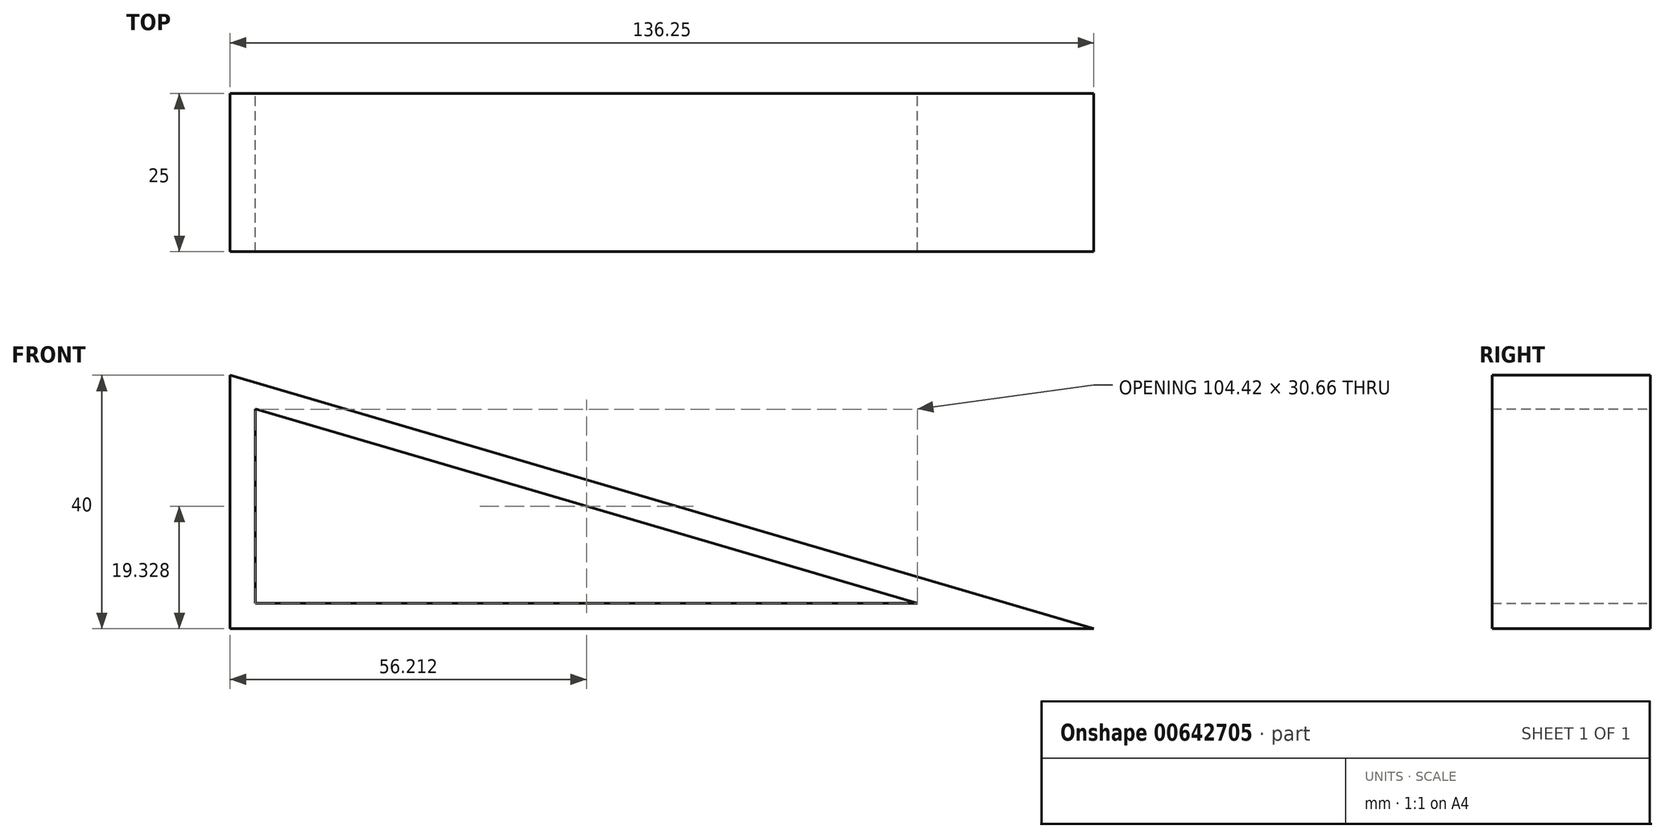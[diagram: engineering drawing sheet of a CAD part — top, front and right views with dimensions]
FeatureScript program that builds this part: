
annotation { "Feature Type Name" : "Feature", "Feature Type Description" : "" }
export const myFeature = defineFeature(function(context is Context, id is Id, definition is map)
    precondition{}
    {
        {
            var Q0;
            Q0=qCreatedBy(makeId("Front.planeOp"),FACE);
            var sketch = newSketch(context, id + "F0", { "sketchPlane" : qUnion([Q0])});
            skLineSegment(sketch, "E0", {"start": v(0, 0) * mm, "end": v(0, 40) * mm});
            skLineSegment(sketch, "E1", {"start": v(0, 40) * mm, "end": v(136.25, 0) * mm});
            skLineSegment(sketch, "E2", {"start": v(136.25, 0) * mm, "end": v(0, 0) * mm});
            skSolve(sketch);
        }
        {
            var Q0;
            Q0=makeQuery(id+"F0.imprint","IMPRINT",FACE,{"disambiguationData":[TD([[makeQuery(id+"F0.imprint","IMPRINT",EDGE,{"derivedFrom":sQuery(id+"F0.wireOp",EDGE,"E0")}),-1.0]])]});
            extrude(context, id + "F1", {"entities" : qUnion([Q0]), "depth" : 33 * mm, "offsetDistance" : 25 * mm});
        }
        {
            var Q0;
            Q0=makeQuery(id+"F1.opExtrude","SWEPT_BODY",BODY,{"disambiguationData":[OSD([sQuery(id+"F0.wireOp",EDGE,"E0"),sQuery(id+"F0.wireOp",EDGE,"E1"),sQuery(id+"F0.wireOp",EDGE,"E2")])]});
            var Q1;
            Q1=sQuery(id+"F0.wireOp",EDGE,"E2");
            transform(context, id + "F2", {"entities" : qUnion([Q0]), "transformType" : TransformType.ROTATION, "transformAxis" : qUnion([Q1]), "angle" : 90 * degree, "makeCopy" : false});
        }
        {
            var Q0;
            Q0=makeQuery(id+"F1.opExtrude","CAP_FACE",FACE,{"disambiguationData":[OSD([sQuery(id+"F0.wireOp",EDGE,"E0"),sQuery(id+"F0.wireOp",EDGE,"E1"),sQuery(id+"F0.wireOp",EDGE,"E2")])],"isStart":false});
            var Q1;
            Q1=makeQuery(id+"F1.opExtrude","SWEPT_BODY",BODY,{"disambiguationData":[OSD([sQuery(id+"F0.wireOp",EDGE,"E0"),sQuery(id+"F0.wireOp",EDGE,"E1"),sQuery(id+"F0.wireOp",EDGE,"E2")])]});
            shell(context, id + "F3", {"isHollow" : true, "entities" : qUnion([Q0]), "parts" : qUnion([Q1]), "thickness" : 4 * mm});
        }
        {
            var Q0;
            Q0=makeQuery(id+"F1.opExtrude","SWEPT_BODY",BODY,{"disambiguationData":[OSD([sQuery(id+"F0.wireOp",EDGE,"E0"),sQuery(id+"F0.wireOp",EDGE,"E1"),sQuery(id+"F0.wireOp",EDGE,"E2")])]});
            var Q1;
            Q1=sQuery(id+"F0.wireOp",EDGE,"E2");
            transform(context, id + "F4", {"entities" : qUnion([Q0]), "transformType" : TransformType.ROTATION, "transformAxis" : qUnion([Q1]), "angle" : 90 * degree, "oppositeDirection" : true, "makeCopy" : false});
        }
        {
            var Q0;
            Q0=makeQuery(id+"F1.opExtrude","CAP_FACE",FACE,{"disambiguationData":[OSD([sQuery(id+"F0.wireOp",EDGE,"E0"),sQuery(id+"F0.wireOp",EDGE,"E1"),sQuery(id+"F0.wireOp",EDGE,"E2")])],"isStart":false});
            extrude(context, id + "F5", {"entities" : qUnion([Q0]), "operationType" : NewBodyOperationType.INTERSECT, "oppositeDirection" : true, "depth" : 29 * mm, "offsetDistance" : 25 * mm, "hasSecondDirection" : true, "secondDirectionOppositeDirection" : true, "secondDirectionDepth" : 4 * mm});
        }
    });
